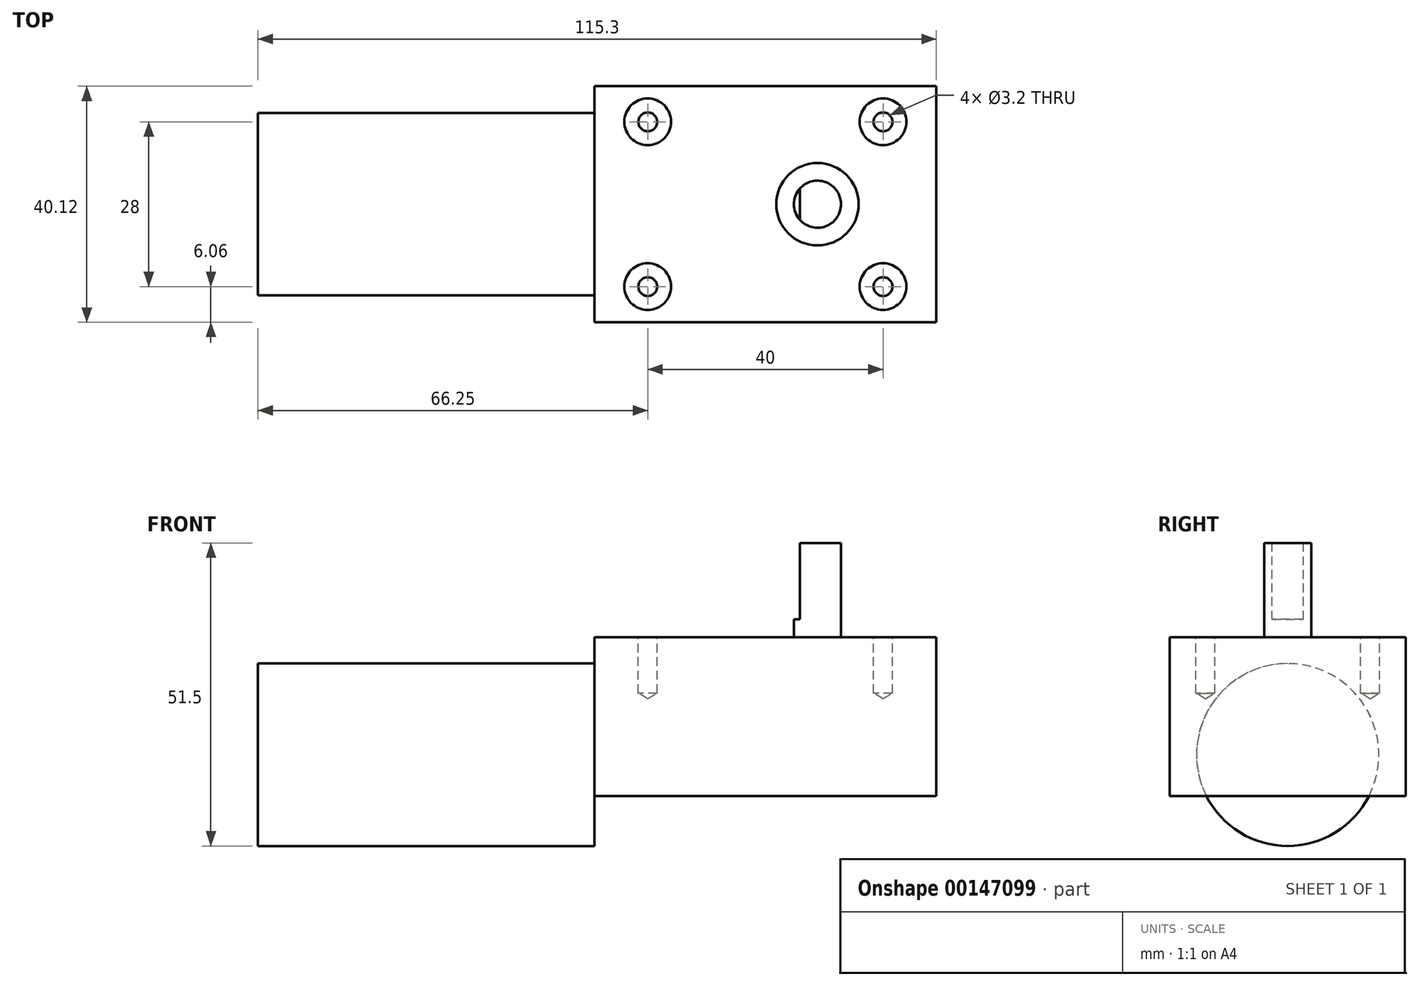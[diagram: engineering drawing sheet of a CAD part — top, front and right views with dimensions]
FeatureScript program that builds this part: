
annotation { "Feature Type Name" : "Feature", "Feature Type Description" : "" }
export const myFeature = defineFeature(function(context is Context, id is Id, definition is map)
    precondition{}
    {
        {
            var Q0;
            Q0=qCreatedBy(makeId("Top.planeOp"),FACE);
            var sketch = newSketch(context, id + "F0", { "sketchPlane" : qUnion([Q0])});
            skLineSegment(sketch, "E0.bottom", {"start": v(0, 0) * mm, "end": v(58.1, 0) * mm});
            skLineSegment(sketch, "E0.top", {"start": v(0, 40.12) * mm, "end": v(58.1, 40.12) * mm});
            skLineSegment(sketch, "E0.left", {"start": v(0, 0) * mm, "end": v(0, 40.12) * mm});
            skLineSegment(sketch, "E0.right", {"start": v(58.1, 0) * mm, "end": v(58.1, 40.12) * mm});
            skSolve(sketch);
        }
        {
            var Q0;
            Q0=makeQuery(id+"F0.imprint","IMPRINT",FACE,{"disambiguationData":[TD([[makeQuery(id+"F0.imprint","IMPRINT",EDGE,{"derivedFrom":sQuery(id+"F0.wireOp",EDGE,"E0.bottom")}),1.0]])]});
            extrude(context, id + "F1", {"entities" : qUnion([Q0]), "depth" : 27 * mm});
        }
        {
            var Q0;
            Q0=makeQuery(id+"F1.opExtrude","CAP_FACE",FACE,{"disambiguationData":[OSD([sQuery(id+"F0.wireOp",EDGE,"E0.bottom"),sQuery(id+"F0.wireOp",EDGE,"E0.top"),sQuery(id+"F0.wireOp",EDGE,"E0.left"),sQuery(id+"F0.wireOp",EDGE,"E0.right")])],"isStart":false});
            var sketch = newSketch(context, id + "F2", { "sketchPlane" : qUnion([Q0])});
            skCircle(sketch, "E1", {"center": v(9.05, 6.06) * mm, "radius": 3.97 * mm});
            skCircle(sketch, "E2", {"center": v(49.05, 6.06) * mm, "radius": 3.97 * mm});
            skCircle(sketch, "E3", {"center": v(49.05, 34.06) * mm, "radius": 3.97 * mm});
            skCircle(sketch, "E4", {"center": v(9.05, 34.06) * mm, "radius": 3.97 * mm});
            skLineSegment(sketch, "E5", {"start": v(9.05, 34.06) * mm, "end": v(49.05, 34.06) * mm, "construction": true});
            skLineSegment(sketch, "E6", {"start": v(49.05, 6.06) * mm, "end": v(49.05, 34.06) * mm, "construction": true});
            skLineSegment(sketch, "E7", {"start": v(49.05, 6.06) * mm, "end": v(9.05, 6.06) * mm, "construction": true});
            skLineSegment(sketch, "E8", {"start": v(9.05, 6.06) * mm, "end": v(9.05, 34.06) * mm, "construction": true});
            skLineSegment(sketch, "E9", {"start": v(29.05, 6.06) * mm, "end": v(29.05, 0) * mm, "construction": true});
            skLineSegment(sketch, "E10", {"start": v(29.05, 40.12) * mm, "end": v(29.05, 34.06) * mm, "construction": true});
            skCircle(sketch, "E11", {"center": v(37.9, 20.06) * mm, "radius": 7 * mm});
            skLineSegment(sketch, "E12", {"start": v(37.9, 20.06) * mm, "end": v(49.05, 20.06) * mm});
            skSolve(sketch);
        }
        {
            var Q0;
            Q0=makeQuery(id+"F2.imprint","IMPRINT",FACE,{"disambiguationData":[TD([[makeQuery(id+"F2.imprint","IMPRINT",EDGE,{"derivedFrom":sQuery(id+"F2.wireOp",EDGE,"E4")}),1.0]])]});
            var Q1;
            Q1=makeQuery(id+"F2.imprint","IMPRINT",FACE,{"disambiguationData":[TD([[makeQuery(id+"F2.imprint","IMPRINT",EDGE,{"derivedFrom":sQuery(id+"F2.wireOp",EDGE,"E1")}),1.0]])]});
            var Q2;
            Q2=makeQuery(id+"F2.imprint","IMPRINT",FACE,{"disambiguationData":[TD([[makeQuery(id+"F2.imprint","IMPRINT",EDGE,{"derivedFrom":sQuery(id+"F2.wireOp",EDGE,"E2")}),1.0]])]});
            var Q3;
            Q3=makeQuery(id+"F2.imprint","IMPRINT",FACE,{"disambiguationData":[TD([[makeQuery(id+"F2.imprint","IMPRINT",EDGE,{"derivedFrom":sQuery(id+"F2.wireOp",EDGE,"E3")}),1.0]])]});
            var Q4;
            Q4=makeQuery(id+"F2.imprint","IMPRINT",FACE,{"disambiguationData":[TD([[makeQuery(id+"F2.imprint","IMPRINT",EDGE,{"derivedFrom":sQuery(id+"F2.wireOp",EDGE,"E11")}),1.0]])]});
            extrude(context, id + "F3", {"entities" : qUnion([Q0, Q1, Q2, Q3, Q4]), "operationType" : NewBodyOperationType.ADD, "depth" : 2 / 645.16 * mm});
        }
        {
            var Q0;
            Q0=makeQuery(id+"F3.opExtrude","CAP_FACE",FACE,{"disambiguationData":[OSD([sQuery(id+"F2.wireOp",EDGE,"E4")])],"isStart":false});
            var sketch = newSketch(context, id + "F4", { "sketchPlane" : qUnion([Q0])});
            skPoint(sketch, "E13", {"position": v(9.05, 34.06) * mm});
            skPoint(sketch, "E14", {"position": v(49.05, 34.06) * mm});
            skPoint(sketch, "E15", {"position": v(49.05, 6.06) * mm});
            skPoint(sketch, "E16", {"position": v(9.05, 6.06) * mm});
            skSolve(sketch);
        }
        {
            var Q0;
            Q0=sQuery(id+"F4.wireOp",VERTEX,"E13");
            var Q1;
            Q1=makeQuery(id+"F1.opExtrude","SWEPT_BODY",BODY,{"disambiguationData":[OSD([sQuery(id+"F0.wireOp",EDGE,"E0.bottom"),sQuery(id+"F0.wireOp",EDGE,"E0.top"),sQuery(id+"F0.wireOp",EDGE,"E0.left"),sQuery(id+"F0.wireOp",EDGE,"E0.right")])]});
            hole(context, id + "F5", {"style" : HoleStyle.SIMPLE, "endStyle" : HoleEndStyle.BLIND, "standardTappedOrClearance" : lookupTablePath({ "standard" : "ISO", "engagement" : "75%", "pitch" : "0.75 mm", "size" : "M4", "type" : "Tapped" }), "standardBlindInLast" : lookupTablePath({ "standard" : "ISO", "engagement" : "75%", "pitch" : "0.75 mm", "size" : "M4", "type" : "Tapped" }), "holeDiameter" : 3.2 * mm, "holeDepth" : 9.52 * mm, "startFromSketch" : true, "locations" : qUnion([Q0]), "scope" : qUnion([Q1])});
        }
        {
            var Q0;
            Q0=sQuery(id+"F4.wireOp",VERTEX,"E14");
            var Q1;
            Q1=makeQuery(id+"F1.opExtrude","SWEPT_BODY",BODY,{"disambiguationData":[OSD([sQuery(id+"F0.wireOp",EDGE,"E0.bottom"),sQuery(id+"F0.wireOp",EDGE,"E0.top"),sQuery(id+"F0.wireOp",EDGE,"E0.left"),sQuery(id+"F0.wireOp",EDGE,"E0.right")])]});
            hole(context, id + "F6", {"style" : HoleStyle.SIMPLE, "endStyle" : HoleEndStyle.BLIND, "standardTappedOrClearance" : lookupTablePath({ "standard" : "ISO", "engagement" : "75%", "pitch" : "0.75 mm", "size" : "M4", "type" : "Tapped" }), "standardBlindInLast" : lookupTablePath({ "standard" : "ISO", "engagement" : "75%", "pitch" : "0.75 mm", "size" : "M4", "type" : "Tapped" }), "holeDiameter" : 3.2 * mm, "holeDepth" : 9.52 * mm, "startFromSketch" : true, "locations" : qUnion([Q0]), "scope" : qUnion([Q1])});
        }
        {
            var Q0;
            Q0=sQuery(id+"F4.wireOp",VERTEX,"E15");
            var Q1;
            Q1=makeQuery(id+"F1.opExtrude","SWEPT_BODY",BODY,{"disambiguationData":[OSD([sQuery(id+"F0.wireOp",EDGE,"E0.bottom"),sQuery(id+"F0.wireOp",EDGE,"E0.top"),sQuery(id+"F0.wireOp",EDGE,"E0.left"),sQuery(id+"F0.wireOp",EDGE,"E0.right")])]});
            hole(context, id + "F7", {"style" : HoleStyle.SIMPLE, "endStyle" : HoleEndStyle.BLIND, "standardTappedOrClearance" : lookupTablePath({ "standard" : "ISO", "engagement" : "75%", "pitch" : "0.75 mm", "size" : "M4", "type" : "Tapped" }), "standardBlindInLast" : lookupTablePath({ "standard" : "ISO", "engagement" : "75%", "pitch" : "0.75 mm", "size" : "M4", "type" : "Tapped" }), "holeDiameter" : 3.2 * mm, "holeDepth" : 9.52 * mm, "startFromSketch" : true, "locations" : qUnion([Q0]), "scope" : qUnion([Q1])});
        }
        {
            var Q0;
            Q0=sQuery(id+"F4.wireOp",VERTEX,"E16");
            var Q1;
            Q1=makeQuery(id+"F1.opExtrude","SWEPT_BODY",BODY,{"disambiguationData":[OSD([sQuery(id+"F0.wireOp",EDGE,"E0.bottom"),sQuery(id+"F0.wireOp",EDGE,"E0.top"),sQuery(id+"F0.wireOp",EDGE,"E0.left"),sQuery(id+"F0.wireOp",EDGE,"E0.right")])]});
            hole(context, id + "F8", {"style" : HoleStyle.SIMPLE, "endStyle" : HoleEndStyle.BLIND, "standardTappedOrClearance" : lookupTablePath({ "standard" : "ISO", "engagement" : "75%", "pitch" : "0.75 mm", "size" : "M4", "type" : "Tapped" }), "standardBlindInLast" : lookupTablePath({ "standard" : "ISO", "engagement" : "75%", "pitch" : "0.75 mm", "size" : "M4", "type" : "Tapped" }), "holeDiameter" : 3.2 * mm, "holeDepth" : 9.52 * mm, "startFromSketch" : true, "locations" : qUnion([Q0]), "scope" : qUnion([Q1])});
        }
        {
            var Q0;
            Q0=makeQuery(id+"F3.opExtrude","CAP_FACE",FACE,{"disambiguationData":[OSD([sQuery(id+"F2.wireOp",EDGE,"E11")])],"isStart":false});
            var sketch = newSketch(context, id + "F9", { "sketchPlane" : qUnion([Q0])});
            skCircle(sketch, "E17", {"center": v(37.9, 20.06) * mm, "radius": 4 * mm});
            skSolve(sketch);
        }
        {
            var Q0;
            Q0=makeQuery(id+"F9.imprint","IMPRINT",FACE,{"disambiguationData":[TD([[makeQuery(id+"F9.imprint","IMPRINT",EDGE,{"derivedFrom":sQuery(id+"F9.wireOp",EDGE,"E17")}),1.0]])]});
            extrude(context, id + "F10", {"entities" : qUnion([Q0]), "operationType" : NewBodyOperationType.ADD, "depth" : 16 * mm});
        }
        {
            var Q0;
            Q0=makeQuery(id+"F10.opExtrude","CAP_FACE",FACE,{"disambiguationData":[OSD([sQuery(id+"F9.wireOp",EDGE,"E17")])],"isStart":false});
            var sketch = newSketch(context, id + "F11", { "sketchPlane" : qUnion([Q0])});
            skCircle(sketch, "E18", {"center": v(37.9, 20.06) * mm, "radius": 4 * mm});
            skLineSegment(sketch, "E19", {"start": v(34.9, 17.41) * mm, "end": v(34.9, 22.7) * mm});
            skLineSegment(sketch, "E20", {"start": v(37.9, 20.06) * mm, "end": v(34.9, 20.06) * mm, "construction": true});
            skPoint(sketch, "E21.orphan", {"position": v(34.9, 12.02) * mm});
            skPoint(sketch, "E22.orphan", {"position": v(34.9, 28.1) * mm});
            skLineSegment(sketch, "E23", {"start": v(34.9, 20.06) * mm, "end": v(33.9, 20.06) * mm, "construction": true});
            skSolve(sketch);
        }
        {
            var Q0;
            {var subQ0=sQuery(id+"F11.wireOp",EDGE,"E19");Q0=makeQuery(id+"F11.imprint","IMPRINT",FACE,{"disambiguationData":[TD([[makeQuery(id+"F11.imprint","IMPRINT",EDGE,{"derivedFrom":subQ0}),1.0]])]});}
            extrude(context, id + "F12", {"entities" : qUnion([Q0]), "operationType" : NewBodyOperationType.REMOVE, "oppositeDirection" : true, "depth" : 13 * mm});
        }
        {
            var Q0;
            Q0=makeQuery(id+"F1.opExtrude","SWEPT_FACE",FACE,{"disambiguationData":[OSD([sQuery(id+"F0.wireOp",EDGE,"E0.left")])]});
            var sketch = newSketch(context, id + "F13", { "sketchPlane" : qUnion([Q0])});
            skCircle(sketch, "E24", {"center": v(-20.06, 7) * mm, "radius": 15.5 * mm});
            skLineSegment(sketch, "E25", {"start": v(-20.06, 27) * mm, "end": v(-20.06, 7) * mm, "construction": true});
            skSolve(sketch);
        }
        {
            var Q0;
            {var subQ0=sQuery(id+"F13.wireOp",EDGE,"E24");var subQ1=makeQuery(id+"F1.opExtrude","CAP_EDGE",EDGE,{"disambiguationData":[OSD([sQuery(id+"F0.wireOp",EDGE,"E0.left")])],"isStart":true});var subQ2=makeQuery(id+"F13.imprint","INTERSECT",VERTEX,{"disambiguationData":[OD(0.0)],"derivedFrom":[subQ1,subQ0]});Q0=makeQuery(id+"F13.imprint","IMPRINT",FACE,{"disambiguationData":[TD([[makeQuery(id+"F13.imprint","IMPRINT",EDGE,{"disambiguationData":[TD([[subQ2,-1.0]])],"derivedFrom":subQ0}),1.0]])]});}
            var Q1;
            {var subQ0=sQuery(id+"F13.wireOp",EDGE,"E24");var subQ1=makeQuery(id+"F1.opExtrude","CAP_EDGE",EDGE,{"disambiguationData":[OSD([sQuery(id+"F0.wireOp",EDGE,"E0.left")])],"isStart":true});var subQ2=makeQuery(id+"F13.imprint","INTERSECT",VERTEX,{"disambiguationData":[OD(0.0)],"derivedFrom":[subQ1,subQ0]});Q1=makeQuery(id+"F13.imprint","IMPRINT",FACE,{"disambiguationData":[TD([[makeQuery(id+"F13.imprint","IMPRINT",EDGE,{"disambiguationData":[TD([[subQ2,1.0]])],"derivedFrom":subQ0}),1.0]])]});}
            extrude(context, id + "F14", {"entities" : qUnion([Q0, Q1]), "operationType" : NewBodyOperationType.ADD, "depth" : 57.2 * mm});
        }
    });
